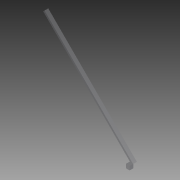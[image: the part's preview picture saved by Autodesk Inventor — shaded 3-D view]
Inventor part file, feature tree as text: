
AUTODESK INVENTOR PART (.ipt)
format: ipt  version: 2013 (Build 170138000, 138)  size: 76,800 bytes
history: native  units: in
note: dims shown in document units (in); Inventor stores cm internally (conversion verified against a paired STEP export)
features: extrude x1, reference x1
ambient origin geometry x8: Origin, YZ Plane, XZ Plane, XY Plane, X Axis, Y Axis, Z Axis, Center Point
bodies: Solid1 (feature_tree)
feature tree (2):
  extrude  "Extrusion1"  Depth=0.25in TaperAngle=0.0deg
  reference  "Reference1"
